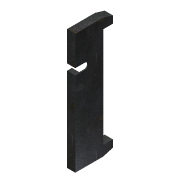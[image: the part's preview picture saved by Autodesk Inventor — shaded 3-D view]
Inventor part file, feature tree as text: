
AUTODESK INVENTOR PART (.ipt)
format: ipt  version: 2016 (Build 200138000, 138)  size: 116,736 bytes
history: native  units: mm
features: extrude x2, sketch x2
ambient origin geometry x8: Origin, YZ Plane, XZ Plane, XY Plane, X Axis, Y Axis, Z Axis, Center Point
bodies: Body1 (feature_tree)
feature tree (4):
  extrude  "Extrusion2"  Depth=13.0mm
  extrude  "Extrusion3"  Depth=16.0mm
  sketch  "Sketch1"  dims[d8=62.0mm d10=13.0mm]
  sketch  "Sketch2"  dims[d12=17.0mm d13=0.0mm d14=16.0mm d15=9.0mm d19=15.0mm d20=0.0mm d21=15.0mm d22=15.0mm d23=32.0mm]
